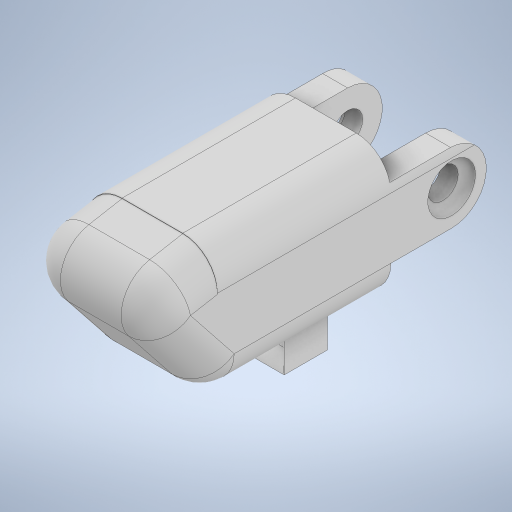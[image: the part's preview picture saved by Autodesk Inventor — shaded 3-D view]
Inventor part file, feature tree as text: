
AUTODESK INVENTOR PART (.ipt)
format: ipt  version: 2024 (Build 280153000, 153)  size: 368,128 bytes
history: native  units: mm
features: extrude x7, sketch x7, fillet x4, other x1
ambient origin geometry x8: Origin, YZ Plane, XZ Plane, XY Plane, X Axis, Y Axis, Z Axis, Center Point
bodies: Body1 (feature_tree), Body2 (feature_tree)
feature tree (19):
  other  "Твердое тело1"
  extrude  "Выдавливание1"  Depth=20.0mm
  extrude  "Выдавливание2"  Depth=15.0mm
  extrude  "Выдавливание3"  Depth=15.0mm TaperAngle=0.0deg
  extrude  "Выдавливание4"  Depth=8.0mm
  fillet  "Сопряжение1"  Radius=11.0mm
  fillet  "Сопряжение2"  Radius=3.0mm
  extrude  "Выдавливание5"  Depth=4.0mm
  extrude  "Выдавливание6"  Depth=4.0mm
  fillet  "Сопряжение3"  Radius=3.5mm
  fillet  "Сопряжение4"  Radius=15.0mm
  extrude  "Выдавливание7"  Depth=7.0mm
  sketch  "Эскиз1"
  sketch  "Эскиз2"
  sketch  "Эскиз3"
  sketch  "Эскиз4"
  sketch  "Эскиз5"
  sketch  "Эскиз6"
  sketch  "Эскиз7"
